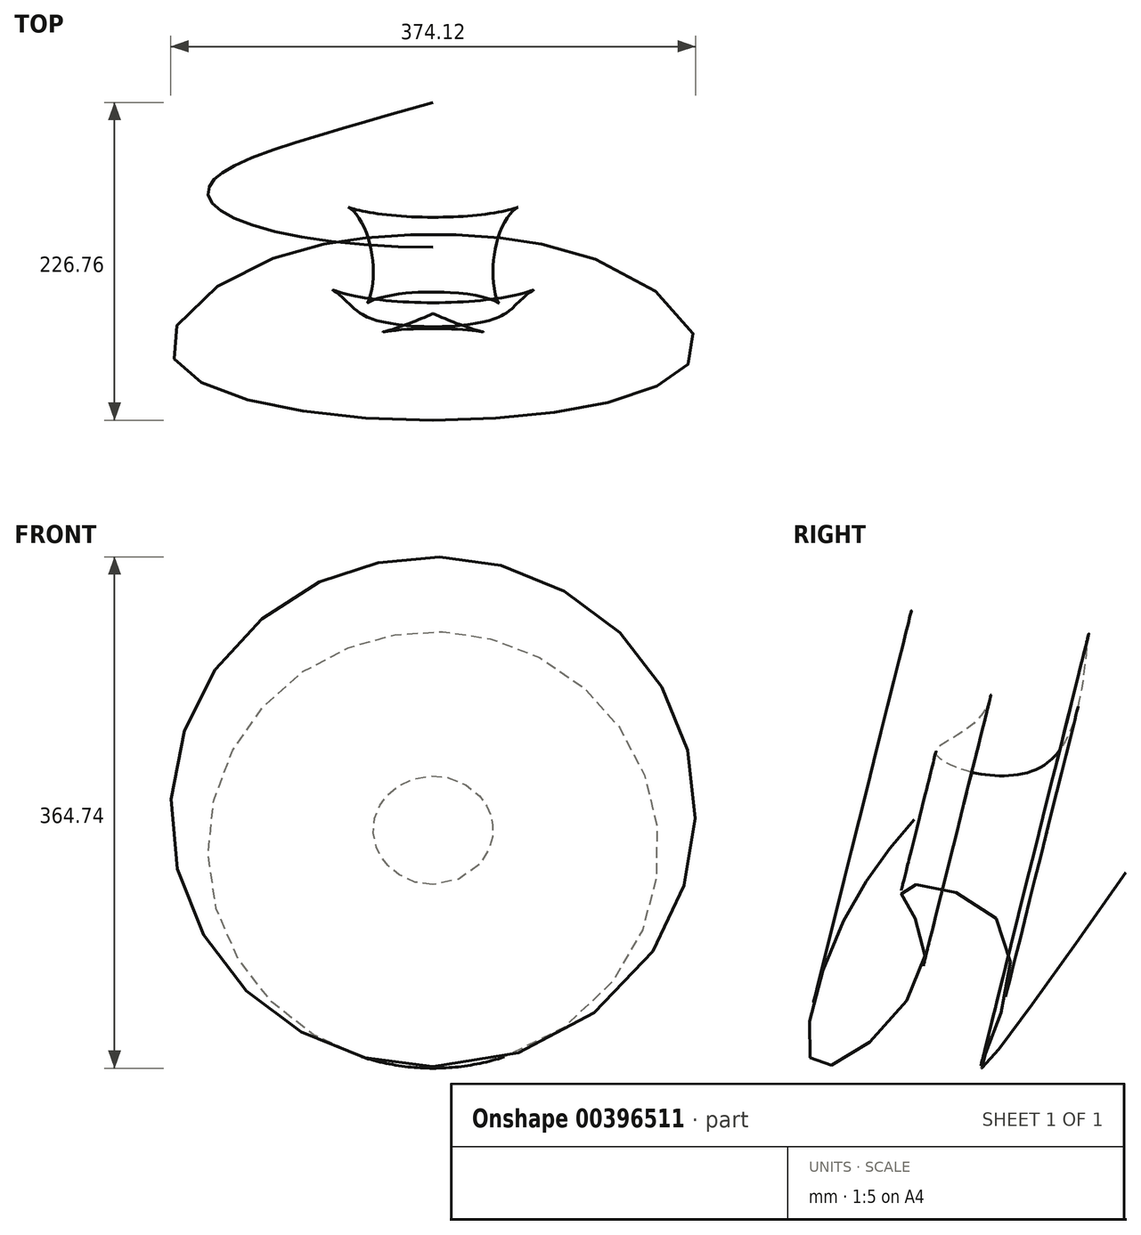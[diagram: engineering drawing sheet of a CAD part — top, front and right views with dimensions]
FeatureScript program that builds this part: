
annotation { "Feature Type Name" : "Feature", "Feature Type Description" : "" }
export const myFeature = defineFeature(function(context is Context, id is Id, definition is map)
    precondition{}
    {
        {
            var Q0;
            Q0=qCreatedBy(makeId("Right.planeOp"),FACE);
            var sketch = newSketch(context, id + "F0", { "sketchPlane" : qUnion([Q0])});
            skLineSegment(sketch, "E0", {"start": v(-66.88, 37.64) * mm, "end": v(83.9, 0) * mm});
            skFitSpline(sketch, "E1", {"points": [v(-66.88, 37.64) * mm, v(-122.06, -45.24) * mm, v(-134.88, -138.18) * mm, v(-59.08, -58.8) * mm, v(-75.33, -11.49) * mm, v(-2.4, -41.98) * mm, v(-19.45, -138.7) * mm, v(83.9, 0) * mm], "startDerivative": vector(-399.8, -467.45) * mm, "endDerivative": vector(826.43, 1178.11) * mm});
            skSolve(sketch);
        }
        {
            var Q0;
            Q0=makeQuery(id+"F0.imprint","IMPRINT",FACE,{"disambiguationData":[TD([[makeQuery(id+"F0.imprint","IMPRINT",EDGE,{"derivedFrom":sQuery(id+"F0.wireOp",EDGE,"E0")}),-1.0]])]});
            var Q1;
            Q1=sQuery(id+"F0.wireOp",EDGE,"E0");
            revolve(context, id + "F1", {"entities" : qUnion([Q0]), "axis" : qUnion([Q1]), "revolveType" : RevolveType.FULL});
        }
    });
